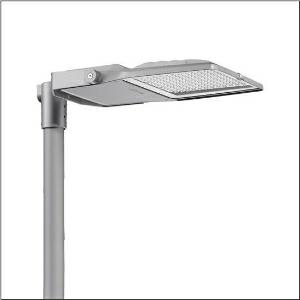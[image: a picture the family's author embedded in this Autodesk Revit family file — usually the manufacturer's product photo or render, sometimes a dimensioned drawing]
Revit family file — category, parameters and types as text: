
# Revit family: floodlight_fl_21_midi___pl61_5xa7786e2c3a_519c
name_source: partatom
category: Lighting Fixtures
units: mm (PartAtom-declared; Revit-internal decimal feet)

## family parameters
Cut with Voids When Loaded = No
Host = Face
Light Source = No
Part Type = Normal
Room Calculation Point = No
Round Connector Dimension = Use Diameter
Shared = No

## types (1)
- --- (1 x LED, 26450 lm, 212.4 W, 3000K)
    Apparent Load = 212 VA
    CIE Flux Codes = 33 65 98 100 100
    Color Rendering = 70
    Color Temperature = 3000K
    Default Elevation = 1800 mm
    Description = Floodlight FL 21 midi, floodlight, primary light control with lens, of PMMA, primary optical cover: protective disc, of toughened safety glass, transparent, light distribution: PL61, light emission: direct distribution, installation type: surface-mounted, LED, High Power LED, rated luminous flux: 26.450lm, luminous efficacy: 125lm/W, light colour: 730, colour temperature: 3000K, control gear: Smart Interface (Zhaga), control: flexible luminous flux parameterisation, time-dependent luminous flux control, constant luminous flux control, overheat protection, pre-setting: logarithmic dimming characteristic, with terminal, 6-pole, mains connection: 220..240V, AC, 50/60Hz, start of lifetime: 212W, end of service life: 231W, reduction: 95W, luminaire housing, of diecast aluminium, powder-coated, SITECO metallic grey (DB 702S), corrosivity category C5 mid according to DIN EN ISO 12944, suitable for swimming pools, chlorine-resistant, sealing non-destructively replaceable, please order mast flange separately, mast bracket, of steel, galvanised, powder-coated, SITECO metallic grey (DB 702S), Smart Interface below and above, protection rating (complete): IP66, insulation class (complete): insulation class II (safety insulation), certification: CE, ENEC, VDE, protection symbol: D, impact resistance: IK08, permissible operating ambient temperature: -40..+40°C, permissible operating ambient temperature for outdoor applications: -40..+50°C, standard: DIN EN 12944, LABS conformity tested according to VDMA 24364:2018-05, packaging unit: 1 piece

Light Distribution: PL61
    Height = 76 mm
    Lamp = 1 x LED
    Lamp Light Flux = 26450 lm
    Lamp Power = 212.4 W
    Lamp count = 1
    Length = 657 mm
    Luminous efficacy = 125 lm/W
    Manufacturer = Siteco
    ModVariant = No
    Model = 5XA7786E2C3A
    Number of Poles = 1
    OnlyDefault = Yes
    Power Factor = 1
    Product Name = Floodlight FL 21 midi | PL61
    Product group = floodlight | pylon annexe
    ProductGroupID = 6201
    Protection Class = Protection class II
    Protection Degree = IP 66
    RLX_Detail_Level = 1
    RLX_Emergency_Light_Flux = 0 lm
    RLX_Emergency_Type = 0
    RLX_Emergency_Type_DB = No
    RlxData = <blob elided: 153837 chars, md5=4243eba4>
    Socket = socket
    Standby Power = 0 W
    System Light Flux = 26450 lm
    System Power = 212 W
    Type Comments = factory setting: luminous flux: 100 % | dim-lin: 254 | 710 mA
    Type Image = l_1007123.jpg
    URL = http://relux.com
    VarID = @adj_191541
    Voltage = 0 V
    Weight = 0.00 kg
    Width = 442 mm

## geometry (parser evidence)
native form markers: Blend x4, Sweep x13
no freeform markers — native parametric forms only
